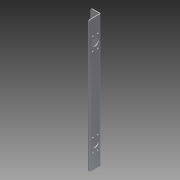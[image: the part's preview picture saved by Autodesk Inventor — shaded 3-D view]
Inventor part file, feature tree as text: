
AUTODESK INVENTOR PART (.ipt)
format: ipt  version: 2014 SP1 (Build 180222100, 222)  size: 314,368 bytes
history: native  units: in
note: dims shown in document units (in); Inventor stores cm internally (conversion verified against a paired STEP export)
features: other x6, sketch x4, sheet_metal_op x2, plane x2, chamfer x1
ambient origin geometry x8: Origin, YZ Plane, XZ Plane, XY Plane, X Axis, Y Axis, Z Axis, Center Point
bodies: Solid1 (feature_tree)
feature tree (15):
  sketch  "Sketch1"  dims[d0=3.1914in]
  sheet_metal_op  "Face1"
  sheet_metal_op  "Fold1"
  other  "Work Axis1"
  chamfer  "Corner Round1"
  other  "Plate1"
  sketch  "Sketch2"  dims[d1=20.0in]
  sketch  "Sketch3"  dims[d2=1.75in]
  plane  "Work Plane1"
  plane  "Work Plane2"
  sketch  "Sketch4"  dims[d3=0.01in d4=0.25in d5=0.25in d6=11.811in d8=0.6638in d9=0.3937in d11=1.0in d13=0.125in d14=0.125in d15=0.0625in d16=0.25in d17=0.125in d18=90.0deg d19=0.05in d20=1.125in d21=0.875in d22=13.35in d23=0.125in d24=0.0in d25=0.266in d26=0.266in d31=0.55in d32=0.125in d33=0.0in d34=4.5in d35=0.25in d36=0.75in d37=0.25in d38=0.25in d39=0.375in d40=5.1181in d42=0.75in d43=0.3937in d45=1.0in d47=0.25in d48=0.375in d49=0.125in d50=0.0in d51=0.75in d52=0.75in d53=0.25in d54=0.25in d56=0.266in d57=0.75in d58=0.266in d59=1.0in d60=0.875in d61=0.875in d62=1.5in d63=4.7244in d65=1.5455in d66=0.3937in d68=1.0in]
  other  "Cut1"
  other  "Cut2"
  other  "Cut3"
  other  "Definition1"
